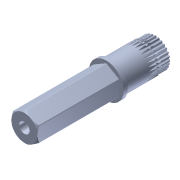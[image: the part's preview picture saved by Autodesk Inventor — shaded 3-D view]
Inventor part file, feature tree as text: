
AUTODESK INVENTOR PART (.ipt)
format: ipt  version: 2013 (Build 170138000, 138)  size: 1,364,480 bytes
history: native  units: in
note: dims shown in document units (in); Inventor stores cm internally (conversion verified against a paired STEP export)
features: fillet x1, other x1, imported_body x1
ambient origin geometry x8: Origin, YZ Plane, XZ Plane, XY Plane, X Axis, Y Axis, Z Axis, Center Point
feature tree (3):
  fillet  "Fillet5"  [1 undecoded]
  other  "217-2625-003 Rev11"
  imported_body  "Base1"
note: 1 required parameter value undecoded (feature->parameter linkage not recoverable at this tier; creation-order binding heuristic only, values carry confidence <= 0.55)
